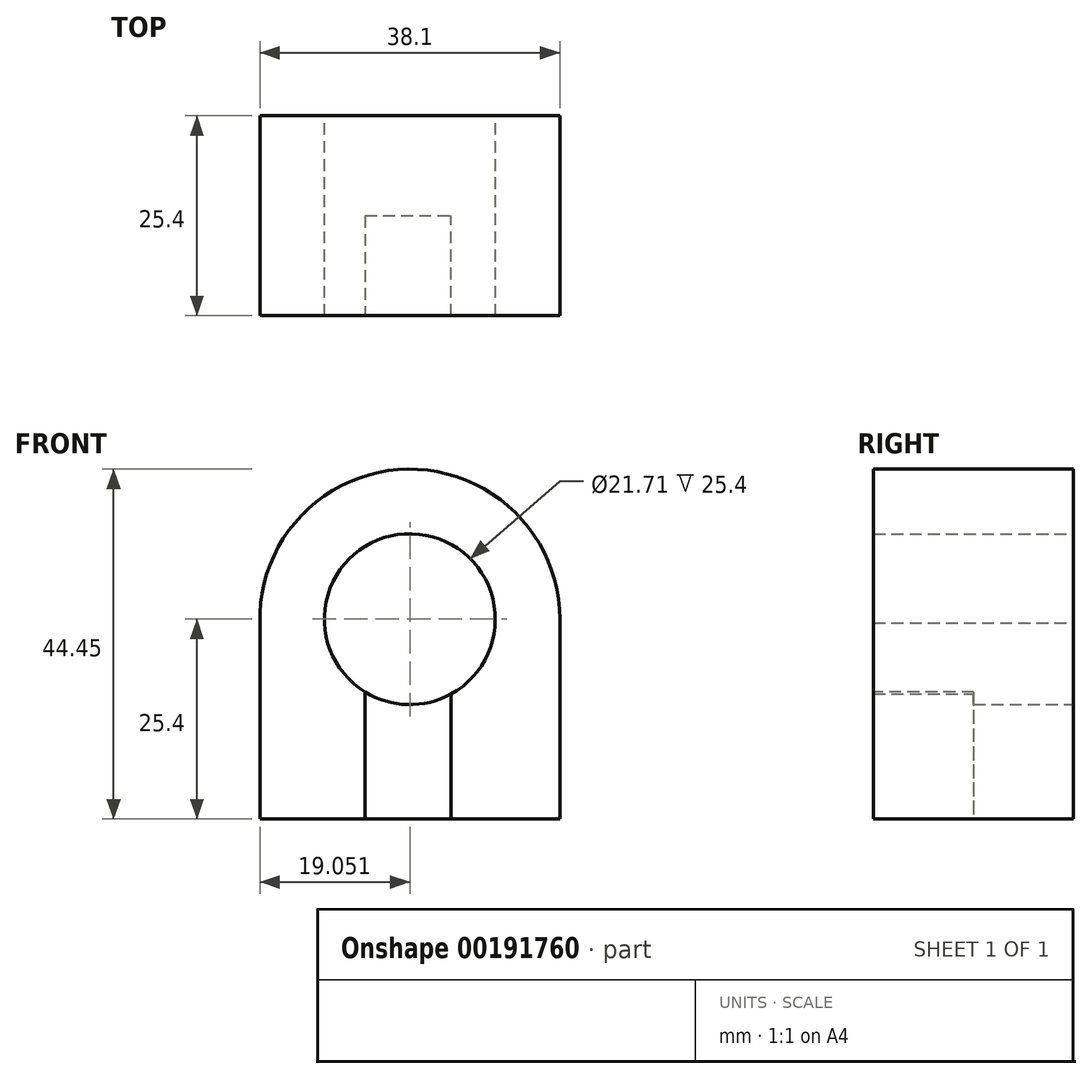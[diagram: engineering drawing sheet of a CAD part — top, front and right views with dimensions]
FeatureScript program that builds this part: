
annotation { "Feature Type Name" : "Feature", "Feature Type Description" : "" }
export const myFeature = defineFeature(function(context is Context, id is Id, definition is map)
    precondition{}
    {
        {
            var Q0;
            Q0=qCreatedBy(makeId("Front.planeOp"),FACE);
            var sketch = newSketch(context, id + "F0", { "sketchPlane" : qUnion([Q0])});
            skLineSegment(sketch, "E0", {"start": v(-16.35, 12.41) * mm, "end": v(-16.35, -12.48) * mm});
            skLineSegment(sketch, "E1", {"start": v(-16.35, -12.48) * mm, "end": v(21.75, -12.48) * mm});
            skLineSegment(sketch, "E2", {"start": v(21.75, -12.48) * mm, "end": v(21.75, 12.92) * mm});
            skArc(sketch, "E3", {"start": v(21.75, 12.92) * mm, "mid": v(2.45, 31.97) * mm, "end": v(-16.35, 12.41) * mm});
            skCircle(sketch, "E4", {"center": v(2.7, 12.92) * mm, "radius": 10.86 * mm});
            skLineSegment(sketch, "E5.bottom", {"start": v(-4.24, 4.57) * mm, "end": v(-4.37, 4.57) * mm});
            skLineSegment(sketch, "E5.top", {"start": v(-4.24, -12.48) * mm, "end": v(-4.37, -12.48) * mm});
            skLineSegment(sketch, "E5.left", {"start": v(-4.24, 4.57) * mm, "end": v(-4.24, -12.48) * mm});
            skLineSegment(sketch, "E5.right", {"start": v(-4.37, 4.57) * mm, "end": v(-4.37, -12.48) * mm});
            skLineSegment(sketch, "E6", {"start": v(9.8, 4.7) * mm, "end": v(9.8, -12.48) * mm});
            skSolve(sketch);
        }
        {
            var Q0;
            Q0 = qSketchRegion(id + "F0", true);
            extrude(context, id + "F1", {"entities" : qUnion([Q0]), "depth" : 25.4 * mm});
        }
        {
            var Q0;
            Q0=makeQuery(id+"F1.opExtrude","CAP_FACE",FACE,{"disambiguationData":[OSD([sQuery(id+"F0.wireOp",EDGE,"E0"),sQuery(id+"F0.wireOp",EDGE,"E1"),sQuery(id+"F0.wireOp",EDGE,"E2"),sQuery(id+"F0.wireOp",EDGE,"E3"),sQuery(id+"F0.wireOp",EDGE,"E4"),sQuery(id+"F0.wireOp",EDGE,"E5.top")])],"isStart":false});
            var sketch = newSketch(context, id + "F2", { "sketchPlane" : qUnion([Q0])});
            skLineSegment(sketch, "E7.bottom", {"start": v(-2.98, 3.67) * mm, "end": v(7.93, 3.67) * mm});
            skLineSegment(sketch, "E7.top", {"start": v(-2.98, -12.48) * mm, "end": v(7.93, -12.48) * mm});
            skLineSegment(sketch, "E7.left", {"start": v(-2.98, 3.67) * mm, "end": v(-2.98, -12.48) * mm});
            skLineSegment(sketch, "E7.right", {"start": v(7.93, 3.67) * mm, "end": v(7.93, -12.48) * mm});
            skSolve(sketch);
        }
        {
            var Q0;
            Q0 = qSketchRegion(id + "F2", true);
            extrude(context, id + "F3", {"entities" : qUnion([Q0]), "operationType" : NewBodyOperationType.REMOVE, "oppositeDirection" : true, "depth" : 12.7 * mm});
        }
    });
